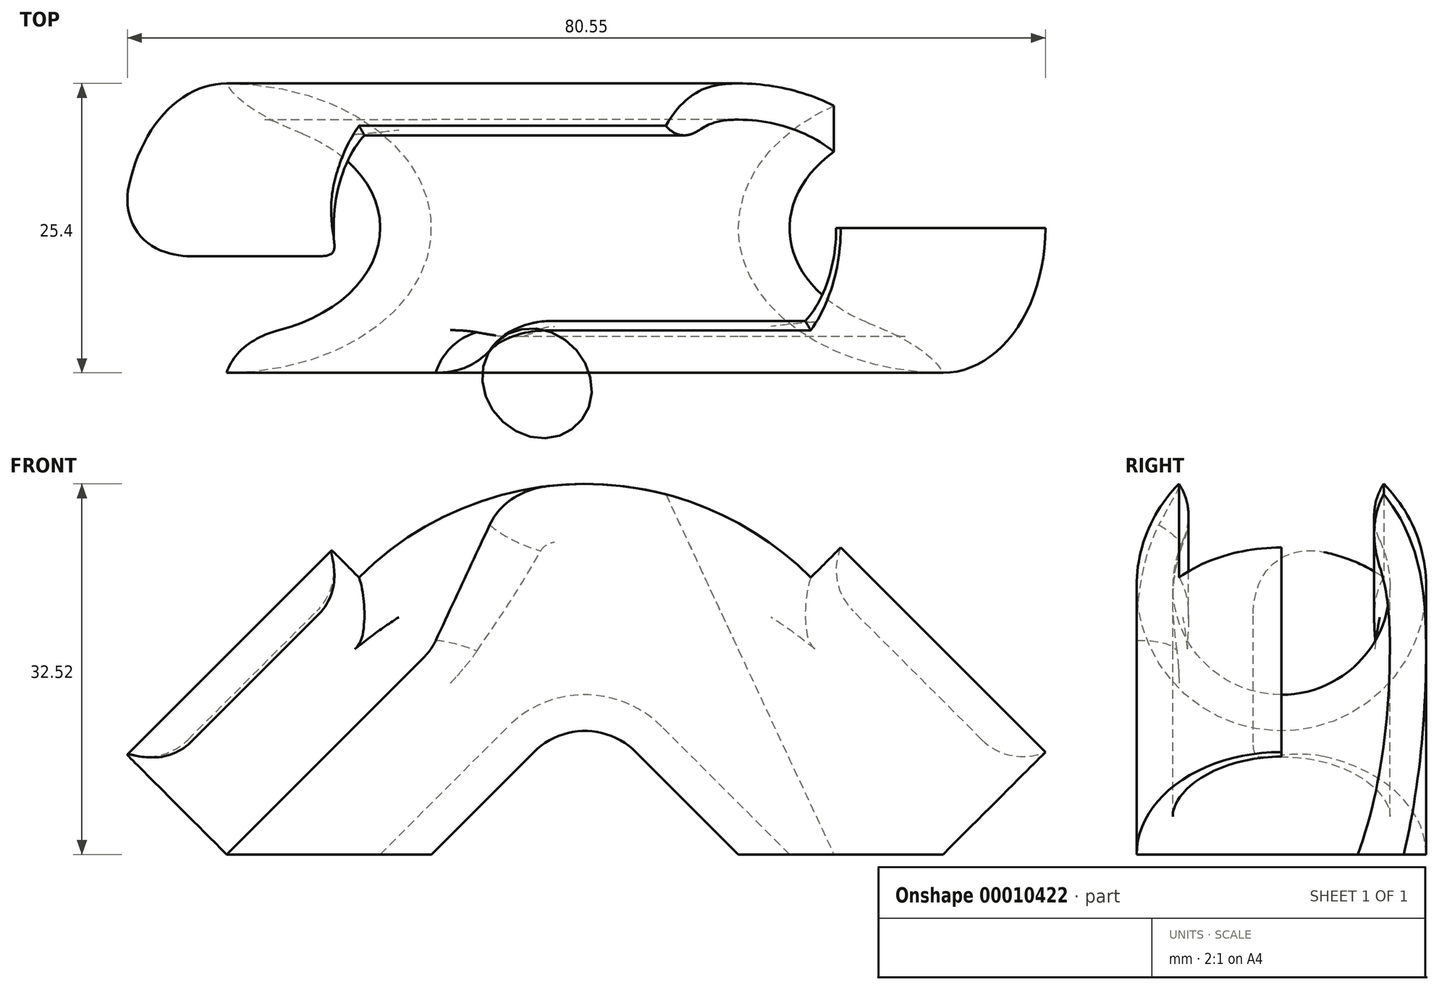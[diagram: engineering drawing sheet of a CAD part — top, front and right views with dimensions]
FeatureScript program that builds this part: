
annotation { "Feature Type Name" : "Feature", "Feature Type Description" : "" }
export const myFeature = defineFeature(function(context is Context, id is Id, definition is map)
    precondition{}
    {
        {
            var Q0;
            Q0=qCreatedBy(makeId("Top.planeOp"),FACE);
            var sketch = newSketch(context, id + "F0", { "sketchPlane" : qUnion([Q0])});
            skArc(sketch, "E0", {"start": v(-19.05, -9.53) * mm, "mid": v(-9.52, 0) * mm, "end": v(-19.05, 9.53) * mm});
            skArc(sketch, "E1", {"start": v(-19.05, -12.7) * mm, "mid": v(-6.35, 0) * mm, "end": v(-19.05, 12.7) * mm});
            skLineSegment(sketch, "E2", {"start": v(-19.05, 12.7) * mm, "end": v(-19.05, -12.7) * mm, "construction": true});
            skLineSegment(sketch, "E3", {"start": v(0, 0) * mm, "end": v(0, 20.3) * mm, "construction": true});
            skArc(sketch, "E4", {"start": v(-19.05, 12.7) * mm, "mid": v(-23.91, 11.73) * mm, "end": v(-28.03, 8.98) * mm});
            skArc(sketch, "E5", {"start": v(-19.05, 9.52) * mm, "mid": v(-22.7, 8.8) * mm, "end": v(-25.79, 6.74) * mm});
            skLineSegment(sketch, "E6", {"start": v(-19.05, 0) * mm, "end": v(-32.52, 13.47) * mm, "construction": true});
            skLineSegment(sketch, "E7", {"start": v(-19.05, 0) * mm, "end": v(-31.74, 0) * mm, "construction": true});
            skLineSegment(sketch, "E8", {"start": v(-28.03, 8.98) * mm, "end": v(-25.79, 6.74) * mm});
            skArc(sketch, "E9.0.MirrorCS", {"start": v(-19.05, -12.7) * mm, "mid": v(-23.91, -11.73) * mm, "end": v(-28.03, -8.98) * mm});
            skArc(sketch, "E10.0.MirrorCS", {"start": v(-19.05, -9.52) * mm, "mid": v(-22.7, -8.8) * mm, "end": v(-25.79, -6.74) * mm});
            skLineSegment(sketch, "E11.0.MirrorCS", {"start": v(-28.03, -8.98) * mm, "end": v(-25.79, -6.74) * mm});
            skSolve(sketch);
        }
        {
            var Q0;
            Q0=makeQuery(id+"F0.imprint","IMPRINT",FACE,{"disambiguationData":[TD([[makeQuery(id+"F0.imprint","IMPRINT",EDGE,{"derivedFrom":sQuery(id+"F0.wireOp",EDGE,"E0")}),-1.0]])]});
            var Q1;
            Q1=sQuery(id+"F0.wireOp",EDGE,"E3");
            revolve(context, id + "F1", {"entities" : qUnion([Q0]), "axis" : qUnion([Q1]), "revolveType" : RevolveType.ONE_DIRECTION, "angle" : 90 * degree});
        }
        {
            var Q0;
            Q0=makeQuery(id+"F1.opRevolve","CAP_FACE",FACE,{"disambiguationData":[OSD([sQuery(id+"F0.wireOp",EDGE,"E0"),sQuery(id+"F0.wireOp",EDGE,"E1"),sQuery(id+"F0.wireOp",EDGE,"f73511b2-d8c9-4d75-855c-6614953555f7"),sQuery(id+"F0.wireOp",EDGE,"cf10e6db-b766-4e5d-b5a8-f7c24e76289a"),sQuery(id+"F0.wireOp",EDGE,"b3be3738-3cac-4f1f-b319-415e728535aa"),sQuery(id+"F0.wireOp",EDGE,"fdc38572-1cb1-49a6-b58a-73fdc4f059a9"),sQuery(id+"F0.wireOp",EDGE,"048312f8-c67a-437b-8760-2d17367ab9db"),sQuery(id+"F0.wireOp",EDGE,"3895a0aa-34ec-4a01-aace-b5ea7a30ab2d")])],"isStart":false});
            extrude(context, id + "F2", {"entities" : qUnion([Q0]), "operationType" : NewBodyOperationType.ADD, "depth" : 38.1 * mm});
        }
        {
            var Q0;
            Q0=makeQuery(id+"F1.opRevolve","CAP_FACE",FACE,{"disambiguationData":[OSD([sQuery(id+"F0.wireOp",EDGE,"E0"),sQuery(id+"F0.wireOp",EDGE,"E1"),sQuery(id+"F0.wireOp",EDGE,"f73511b2-d8c9-4d75-855c-6614953555f7"),sQuery(id+"F0.wireOp",EDGE,"cf10e6db-b766-4e5d-b5a8-f7c24e76289a"),sQuery(id+"F0.wireOp",EDGE,"b3be3738-3cac-4f1f-b319-415e728535aa"),sQuery(id+"F0.wireOp",EDGE,"fdc38572-1cb1-49a6-b58a-73fdc4f059a9"),sQuery(id+"F0.wireOp",EDGE,"048312f8-c67a-437b-8760-2d17367ab9db"),sQuery(id+"F0.wireOp",EDGE,"3895a0aa-34ec-4a01-aace-b5ea7a30ab2d")])],"isStart":true});
            extrude(context, id + "F3", {"entities" : qUnion([Q0]), "operationType" : NewBodyOperationType.ADD, "depth" : 38.1 * mm});
        }
        {
            var Q0;
            Q0=makeQuery(id+"F2.opExtrude","CAP_FACE",FACE,{"disambiguationData":[OSD([sQuery(id+"F0.wireOp",EDGE,"E0"),sQuery(id+"F0.wireOp",EDGE,"E1"),sQuery(id+"F0.wireOp",EDGE,"E4"),sQuery(id+"F0.wireOp",EDGE,"E5"),sQuery(id+"F0.wireOp",EDGE,"E8"),sQuery(id+"F0.wireOp",EDGE,"E9.0.MirrorCS"),sQuery(id+"F0.wireOp",EDGE,"E10.0.MirrorCS"),sQuery(id+"F0.wireOp",EDGE,"E11.0.MirrorCS")])],"isStart":false});
            var sketch = newSketch(context, id + "F4", { "sketchPlane" : qUnion([Q0])});
            skPoint(sketch, "E12", {"position": v(0, 19.05) * mm});
            skSolve(sketch);
        }
        {
            var Q0;
            {var subQ0=sQuery(id+"F0.wireOp",EDGE,"E0");var subQ1=sQuery(id+"F0.wireOp",EDGE,"E5");var subQ2=sQuery(id+"F0.wireOp",EDGE,"E10.0.MirrorCS");Q0=makeQuery(id+"F2.boolean.opBoolean","MERGE",EDGE,{"derivedFrom":[makeQuery(id+"F1.opRevolve","CAP_EDGE",EDGE,{"disambiguationData":[OSD([subQ0,subQ1,subQ2])],"isStart":false}),makeQuery(id+"F2.opExtrude","CAP_EDGE",EDGE,{"disambiguationData":[OSD([subQ0,subQ1,subQ2])],"isStart":true})]});}
            var Q1;
            {var subQ0=sQuery(id+"F0.wireOp",EDGE,"E5");var subQ1=sQuery(id+"F0.wireOp",EDGE,"E8");Q1=makeQuery(id+"F2.boolean.opBoolean","MERGE",VERTEX,{"derivedFrom":[makeQuery(id+"F1.opRevolve","CAP_VERTEX",VERTEX,{"disambiguationData":[OSD([subQ0,subQ1])],"isStart":false}),makeQuery(id+"F2.opExtrude","CAP_VERTEX",VERTEX,{"disambiguationData":[OSD([subQ0,subQ1])],"isStart":true})]});}
            cPlane(context, id + "F5", {"entities" : qUnion([Q0, Q1]), "cplaneType" : CPlaneType.CURVE_POINT, "offset" : 152.4 * mm, "width" : 152.4 * mm, "height" : 152.4 * mm});
        }
        {
            var Q0;
            Q0=qCreatedBy(id+"F5.planeOp",FACE);
            var sketch = newSketch(context, id + "F6", { "sketchPlane" : qUnion([Q0])});
            skLineSegment(sketch, "E13", {"start": v(6.59, 13.47) * mm, "end": v(-44.56, 13.47) * mm, "construction": true});
            skSolve(sketch);
        }
        {
            var Q0;
            Q0=makeQuery(id+"F2.opExtrude","SWEPT_FACE",FACE,{"disambiguationData":[OSD([sQuery(id+"F0.wireOp",EDGE,"E8")])]});
            var Q1;
            Q1=sQuery(id+"F6.wireOp",EDGE,"E13");
            revolve(context, id + "F7", {"operationType" : NewBodyOperationType.REMOVE, "entities" : qUnion([Q0]), "axis" : qUnion([Q1]), "revolveType" : RevolveType.ONE_DIRECTION, "angle" : 45 * degree});
        }
        {
            var Q0;
            Q0=makeQuery(id+"F2.opExtrude","SWEPT_FACE",FACE,{"disambiguationData":[OSD([sQuery(id+"F0.wireOp",EDGE,"E11.0.MirrorCS")])]});
            var Q1;
            Q1=sQuery(id+"F6.wireOp",EDGE,"E13");
            revolve(context, id + "F8", {"operationType" : NewBodyOperationType.ADD, "entities" : qUnion([Q0]), "axis" : qUnion([Q1]), "revolveType" : RevolveType.ONE_DIRECTION, "angle" : 60 * degree});
        }
        {
            var Q0;
            Q0=qCreatedBy(makeId("Front.planeOp"),FACE);
            var sketch = newSketch(context, id + "F9", { "sketchPlane" : qUnion([Q0])});
            skLineSegment(sketch, "E14", {"start": v(-34.9, 31.75) * mm, "end": v(50.8, 31.75) * mm});
            skLineSegment(sketch, "E15", {"start": v(-34.9, 31.75) * mm, "end": v(50.8, 0.56) * mm});
            skPoint(sketch, "E16", {"position": v(0, 19.05) * mm});
            skLineSegment(sketch, "E17", {"start": v(50.8, 31.75) * mm, "end": v(50.8, 0.56) * mm});
            skSolve(sketch);
        }
        {
            var Q0;
            Q0=makeQuery(id+"F9.imprint","IMPRINT",FACE,{"disambiguationData":[TD([[makeQuery(id+"F9.imprint","IMPRINT",EDGE,{"derivedFrom":sQuery(id+"F9.wireOp",EDGE,"E14")}),-1.0]])]});
            extrude(context, id + "F10", {"entities" : qUnion([Q0]), "operationType" : NewBodyOperationType.REMOVE, "endBound" : BoundingType.THROUGH_ALL, "oppositeDirection" : true, "depth" : 25.4 * mm});
        }
        {
            var Q0;
            Q0=makeQuery(id+"F3.opExtrude","CAP_FACE",FACE,{"disambiguationData":[OSD([sQuery(id+"F0.wireOp",EDGE,"E0"),sQuery(id+"F0.wireOp",EDGE,"E1"),sQuery(id+"F0.wireOp",EDGE,"E4"),sQuery(id+"F0.wireOp",EDGE,"E5"),sQuery(id+"F0.wireOp",EDGE,"E8"),sQuery(id+"F0.wireOp",EDGE,"E9.0.MirrorCS"),sQuery(id+"F0.wireOp",EDGE,"E10.0.MirrorCS"),sQuery(id+"F0.wireOp",EDGE,"E11.0.MirrorCS")])],"isStart":false});
            var sketch = newSketch(context, id + "F11", { "sketchPlane" : qUnion([Q0])});
            skPoint(sketch, "E18", {"position": v(-19.05, 0) * mm});
            skSolve(sketch);
        }
        {
            var Q0;
            Q0=makeQuery(id+"F3.opExtrude","SWEPT_FACE",FACE,{"disambiguationData":[OSD([sQuery(id+"F0.wireOp",EDGE,"E8")])]});
            var sketch = newSketch(context, id + "F12", { "sketchPlane" : qUnion([Q0])});
            skLineSegment(sketch, "E19", {"start": v(-13.47, -9.08) * mm, "end": v(-13.47, 14.4) * mm, "construction": true});
            skSolve(sketch);
        }
        {
            var Q0;
            Q0=makeQuery(id+"F3.opExtrude","SWEPT_FACE",FACE,{"disambiguationData":[OSD([sQuery(id+"F0.wireOp",EDGE,"E11.0.MirrorCS")])]});
            var Q1;
            Q1=sQuery(id+"F12.wireOp",EDGE,"E19");
            revolve(context, id + "F13", {"operationType" : NewBodyOperationType.REMOVE, "entities" : qUnion([Q0]), "axis" : qUnion([Q1]), "revolveType" : RevolveType.ONE_DIRECTION, "angle" : 45 * degree});
        }
        {
            var Q0;
            {var subQ0=sQuery(id+"F0.wireOp",EDGE,"E8");Q0=makeQuery(id+"F12.imprint","IMPRINT",FACE,{"disambiguationData":[TD([[makeQuery(id+"F12.imprint","IMPRINT",EDGE,{"derivedFrom":makeQuery(id+"F3.opExtrude","CAP_EDGE",EDGE,{"disambiguationData":[OSD([subQ0])],"isStart":false})}),1.0]])]});}
            var Q1;
            Q1=sQuery(id+"F12.wireOp",EDGE,"E19");
            revolve(context, id + "F14", {"operationType" : NewBodyOperationType.ADD, "entities" : qUnion([Q0]), "axis" : qUnion([Q1]), "revolveType" : RevolveType.ONE_DIRECTION, "angle" : 60 * degree});
        }
        {
            var Q0;
            Q0=qCreatedBy(makeId("Front.planeOp"),FACE);
            var sketch = newSketch(context, id + "F15", { "sketchPlane" : qUnion([Q0])});
            skLineSegment(sketch, "E20", {"start": v(-19.05, 0) * mm, "end": v(-29.14, 27.72) * mm});
            skLineSegment(sketch, "E21", {"start": v(-29.14, 27.72) * mm, "end": v(-29.14, 0) * mm});
            skLineSegment(sketch, "E22", {"start": v(-29.14, 0) * mm, "end": v(-19.05, 0) * mm});
            skSolve(sketch);
        }
        {
            var Q0;
            Q0=makeQuery(id+"F15.imprint","IMPRINT",FACE,{"disambiguationData":[TD([[makeQuery(id+"F15.imprint","IMPRINT",EDGE,{"derivedFrom":sQuery(id+"F15.wireOp",EDGE,"E20")}),1.0]])]});
            extrude(context, id + "F16", {"entities" : qUnion([Q0]), "operationType" : NewBodyOperationType.REMOVE, "endBound" : BoundingType.THROUGH_ALL, "depth" : 25.4 * mm});
        }
        {
            var Q0;
            Q0=qCreatedBy(makeId("Front.planeOp"),FACE);
            var sketch = newSketch(context, id + "F17", { "sketchPlane" : qUnion([Q0])});
            skLineSegment(sketch, "E23", {"start": v(-19.05, -25.4) * mm, "end": v(25.4, 19.05) * mm});
            skLineSegment(sketch, "E24", {"start": v(-44.3, -27.55) * mm, "end": v(-9.15, -62.69) * mm});
            skLineSegment(sketch, "E25", {"start": v(-9.15, -62.69) * mm, "end": v(62.69, 9.15) * mm});
            skLineSegment(sketch, "E26", {"start": v(62.69, 9.15) * mm, "end": v(27.32, 44.52) * mm});
            skLineSegment(sketch, "E27", {"start": v(-19.05, -25.4) * mm, "end": v(-42.14, -25.4) * mm});
            skLineSegment(sketch, "E28", {"start": v(-42.14, -25.4) * mm, "end": v(-44.3, -27.55) * mm});
            skLineSegment(sketch, "E29", {"start": v(25.4, 19.05) * mm, "end": v(25.4, 42.6) * mm});
            skLineSegment(sketch, "E30", {"start": v(25.4, 42.6) * mm, "end": v(27.32, 44.52) * mm});
            skSolve(sketch);
        }
        {
            var Q0;
            Q0 = qSketchRegion(id + "F17", true);
            extrude(context, id + "F18", {"entities" : qUnion([Q0]), "operationType" : NewBodyOperationType.REMOVE, "endBound" : BoundingType.THROUGH_ALL, "oppositeDirection" : true, "depth" : 25.4 * mm, "hasSecondDirection" : true, "secondDirectionBound" : BoundingType.THROUGH_ALL, "secondDirectionOppositeDirection" : false, "secondDirectionDepth" : 25.4 * mm});
        }
        {
            var Q0;
            Q0=makeQuery(id+"F10.boolean.opBoolean","INTERSECT",EDGE,{"derivedFrom":[makeQuery(id+"F1.opRevolve","SWEPT_FACE",FACE,{"disambiguationData":[OSD([sQuery(id+"F0.wireOp",EDGE,"E8")])]}),makeQuery(id+"F10.opExtrude","SWEPT_FACE",FACE,{"disambiguationData":[OSD([sQuery(id+"F9.wireOp",EDGE,"83bf9a25-06dd-49f2-be48-796f3eb4b7b6")])]})]});
            var Q1;
            {var subQ0=sQuery(id+"F0.wireOp",EDGE,"E8");Q1=makeQuery(id+"F10.boolean.opBoolean","MERGE",EDGE,{"derivedFrom":[makeQuery(id+"F7.boolean.opBoolean","COPY",EDGE,{"derivedFrom":makeQuery(id+"F7.opRevolve","CAP_EDGE",EDGE,{"disambiguationData":[OSD([subQ0]),TDD([makeQuery(id+"F2.boolean.opBoolean","MERGE",EDGE,{"derivedFrom":[makeQuery(id+"F1.opRevolve","CAP_EDGE",EDGE,{"disambiguationData":[OSD([subQ0])],"isStart":false}),makeQuery(id+"F2.opExtrude","CAP_EDGE",EDGE,{"disambiguationData":[OSD([subQ0])],"isStart":true})]})])],"isStart":false})}),makeQuery(id+"F10.opExtrude","SWEPT_EDGE",EDGE,{"disambiguationData":[OSD([sQuery(id+"F9.wireOp",EDGE,"83bf9a25-06dd-49f2-be48-796f3eb4b7b6"),sQuery(id+"F9.wireOp",EDGE,"02377960-e664-4dbb-af69-8dd010406927")])]})]});}
            var Q2;
            {var subQ0=sQuery(id+"F0.wireOp",EDGE,"E11.0.MirrorCS");Q2=makeQuery(id+"F16.boolean.opBoolean","MERGE",EDGE,{"derivedFrom":[makeQuery(id+"F13.boolean.opBoolean","COPY",EDGE,{"derivedFrom":makeQuery(id+"F13.opRevolve","CAP_EDGE",EDGE,{"disambiguationData":[OSD([subQ0]),TDD([makeQuery(id+"F3.boolean.opBoolean","MERGE",EDGE,{"derivedFrom":[makeQuery(id+"F1.opRevolve","CAP_EDGE",EDGE,{"disambiguationData":[OSD([subQ0])],"isStart":true}),makeQuery(id+"F3.opExtrude","CAP_EDGE",EDGE,{"disambiguationData":[OSD([subQ0])],"isStart":true})]})])],"isStart":false})}),makeQuery(id+"F16.opExtrude","SWEPT_EDGE",EDGE,{"disambiguationData":[OSD([sQuery(id+"F15.wireOp",EDGE,"E20"),sQuery(id+"F15.wireOp",EDGE,"E22")])]})]});}
            var Q3;
            Q3=makeQuery(id+"F16.boolean.opBoolean","INTERSECT",EDGE,{"derivedFrom":[makeQuery(id+"F1.opRevolve","SWEPT_FACE",FACE,{"disambiguationData":[OSD([sQuery(id+"F0.wireOp",EDGE,"E11.0.MirrorCS")])]}),makeQuery(id+"F16.opExtrude","SWEPT_FACE",FACE,{"disambiguationData":[OSD([sQuery(id+"F15.wireOp",EDGE,"E20")])]})]});
            fillet(context, id + "F19", {"entities" : qUnion([Q0, Q1, Q2, Q3]), "radius" : 5.08 * mm, "tangentPropagation" : true, "allowEdgeOverflow" : false});
        }
        {
            var Q0;
            Q0=makeQuery(id+"F1.opRevolve","SWEPT_EDGE",EDGE,{"disambiguationData":[OSD([sQuery(id+"F0.wireOp",EDGE,"E10.0.MirrorCS"),sQuery(id+"F0.wireOp",EDGE,"E11.0.MirrorCS")])]});
            var Q1;
            Q1=makeQuery(id+"F1.opRevolve","SWEPT_EDGE",EDGE,{"disambiguationData":[OSD([sQuery(id+"F0.wireOp",EDGE,"E5"),sQuery(id+"F0.wireOp",EDGE,"E8")])]});
            var Q2;
            Q2=makeQuery(id+"F8.opRevolve","CAP_EDGE",EDGE,{"disambiguationData":[OSD([sQuery(id+"F0.wireOp",EDGE,"E9.0.MirrorCS"),sQuery(id+"F0.wireOp",EDGE,"E11.0.MirrorCS")])],"isStart":false});
            var Q3;
            Q3=makeQuery(id+"F14.opRevolve","CAP_EDGE",EDGE,{"disambiguationData":[OSD([sQuery(id+"F0.wireOp",EDGE,"E4"),sQuery(id+"F0.wireOp",EDGE,"E8")])],"isStart":false});
            fillet(context, id + "F20", {"entities" : qUnion([Q0, Q1, Q2, Q3]), "radius" : 5.08 * mm, "tangentPropagation" : true, "allowEdgeOverflow" : false});
        }
        {
            var Q0;
            Q0=qCreatedBy(makeId("Top.planeOp"),FACE);
            var sketch = newSketch(context, id + "F21", { "sketchPlane" : qUnion([Q0])});
            skLineSegment(sketch, "E31", {"start": v(0, 0) * mm, "end": v(0, -76.9) * mm, "construction": true});
            skSolve(sketch);
        }
        {
            var Q0;
            Q0=makeQuery(id+"F1.opRevolve","SWEPT_BODY",BODY,{"disambiguationData":[OSD([sQuery(id+"F0.wireOp",EDGE,"E0"),sQuery(id+"F0.wireOp",EDGE,"E1"),sQuery(id+"F0.wireOp",EDGE,"E4"),sQuery(id+"F0.wireOp",EDGE,"E5"),sQuery(id+"F0.wireOp",EDGE,"E8"),sQuery(id+"F0.wireOp",EDGE,"E9.0.MirrorCS"),sQuery(id+"F0.wireOp",EDGE,"E10.0.MirrorCS"),sQuery(id+"F0.wireOp",EDGE,"E11.0.MirrorCS")])]});
            var Q1;
            Q1=sQuery(id+"F21.wireOp",EDGE,"E31");
            transform(context, id + "F22", {"entities" : qUnion([Q0]), "transformType" : TransformType.ROTATION, "transformAxis" : qUnion([Q1]), "angle" : 45 * degree, "oppositeDirection" : true, "makeCopy" : false});
        }
        {
            var Q0;
            {var subQ0=sQuery(id+"F0.wireOp",EDGE,"E5");Q0=makeQuery(id+"F18.boolean.opBoolean","INTERSECT",EDGE,{"derivedFrom":[makeQuery(id+"F14.boolean.opBoolean","MERGE",FACE,{"derivedFrom":[makeQuery(id+"F3.opExtrude","SWEPT_FACE",FACE,{"disambiguationData":[OSD([sQuery(id+"F0.wireOp",EDGE,"E0"),subQ0,sQuery(id+"F0.wireOp",EDGE,"E10.0.MirrorCS")])]}),makeQuery(id+"F14.opRevolve","SWEPT_FACE",FACE,{"disambiguationData":[OSD([subQ0,sQuery(id+"F0.wireOp",EDGE,"E8")])]})]}),makeQuery(id+"F18.opExtrude","SWEPT_FACE",FACE,{"disambiguationData":[OSD([sQuery(id+"F17.wireOp",EDGE,"E27")])]})]});}
            var Q1;
            {var subQ0=sQuery(id+"F0.wireOp",EDGE,"E10.0.MirrorCS");Q1=makeQuery(id+"F18.boolean.opBoolean","INTERSECT",EDGE,{"derivedFrom":[makeQuery(id+"F8.boolean.opBoolean","MERGE",FACE,{"derivedFrom":[makeQuery(id+"F2.opExtrude","SWEPT_FACE",FACE,{"disambiguationData":[OSD([sQuery(id+"F0.wireOp",EDGE,"E0"),sQuery(id+"F0.wireOp",EDGE,"E5"),subQ0])]}),makeQuery(id+"F8.opRevolve","SWEPT_FACE",FACE,{"disambiguationData":[OSD([subQ0,sQuery(id+"F0.wireOp",EDGE,"E11.0.MirrorCS")])]})]}),makeQuery(id+"F18.opExtrude","SWEPT_FACE",FACE,{"disambiguationData":[OSD([sQuery(id+"F17.wireOp",EDGE,"E29")])]})]});}
            var Q2;
            {var subQ0=sQuery(id+"F0.wireOp",EDGE,"E10.0.MirrorCS");var subQ1=sQuery(id+"F0.wireOp",EDGE,"E11.0.MirrorCS");var subQ2=sQuery(id+"F0.wireOp",EDGE,"E0");var subQ3=sQuery(id+"F0.wireOp",EDGE,"E5");Q2=makeQuery(id+"F20.opFillet","MERGE",EDGE,{"derivedFrom":[makeQuery(id+"F8.opRevolve","SWEPT_EDGE",EDGE,{"disambiguationData":[OSD([subQ0,subQ1]),TDD([makeQuery(id+"F2.boolean.opBoolean","MERGE",VERTEX,{"derivedFrom":[makeQuery(id+"F1.opRevolve","CAP_VERTEX",VERTEX,{"disambiguationData":[OSD([subQ0,subQ1])],"isStart":false}),makeQuery(id+"F2.opExtrude","CAP_VERTEX",VERTEX,{"disambiguationData":[OSD([subQ0,subQ1])],"isStart":true})]})])]}),makeQuery(id+"F2.boolean.opBoolean","MERGE",EDGE,{"derivedFrom":[makeQuery(id+"F1.opRevolve","CAP_EDGE",EDGE,{"disambiguationData":[OSD([subQ2,subQ3,subQ0])],"isStart":false}),makeQuery(id+"F2.opExtrude","CAP_EDGE",EDGE,{"disambiguationData":[OSD([subQ2,subQ3,subQ0])],"isStart":true})]})]});}
            var Q3;
            {var subQ0=sQuery(id+"F0.wireOp",EDGE,"E5");var subQ1=sQuery(id+"F0.wireOp",EDGE,"E8");var subQ2=sQuery(id+"F0.wireOp",EDGE,"E0");var subQ3=sQuery(id+"F0.wireOp",EDGE,"E10.0.MirrorCS");Q3=makeQuery(id+"F20.opFillet","MERGE",EDGE,{"derivedFrom":[makeQuery(id+"F14.opRevolve","SWEPT_EDGE",EDGE,{"disambiguationData":[OSD([subQ0,subQ1]),TDD([makeQuery(id+"F12.imprint","INTERSECT",VERTEX,{"derivedFrom":[makeQuery(id+"F3.opExtrude","SWEPT_EDGE",EDGE,{"disambiguationData":[OSD([subQ0,subQ1])]}),makeQuery(id+"F3.boolean.opBoolean","MERGE",EDGE,{"derivedFrom":[makeQuery(id+"F1.opRevolve","CAP_EDGE",EDGE,{"disambiguationData":[OSD([subQ1])],"isStart":true}),makeQuery(id+"F3.opExtrude","CAP_EDGE",EDGE,{"disambiguationData":[OSD([subQ1])],"isStart":true})]})]})])]}),makeQuery(id+"F13.boolean.opBoolean","COPY",EDGE,{"derivedFrom":makeQuery(id+"F3.boolean.opBoolean","MERGE",EDGE,{"derivedFrom":[makeQuery(id+"F1.opRevolve","CAP_EDGE",EDGE,{"disambiguationData":[OSD([subQ2,subQ0,subQ3])],"isStart":true}),makeQuery(id+"F3.opExtrude","CAP_EDGE",EDGE,{"disambiguationData":[OSD([subQ2,subQ0,subQ3])],"isStart":true})]})})]});}
            fillet(context, id + "F23", {"entities" : qUnion([Q0, Q1, Q2, Q3]), "radius" : 5.08 * mm, "tangentPropagation" : true, "allowEdgeOverflow" : false});
        }
    });
